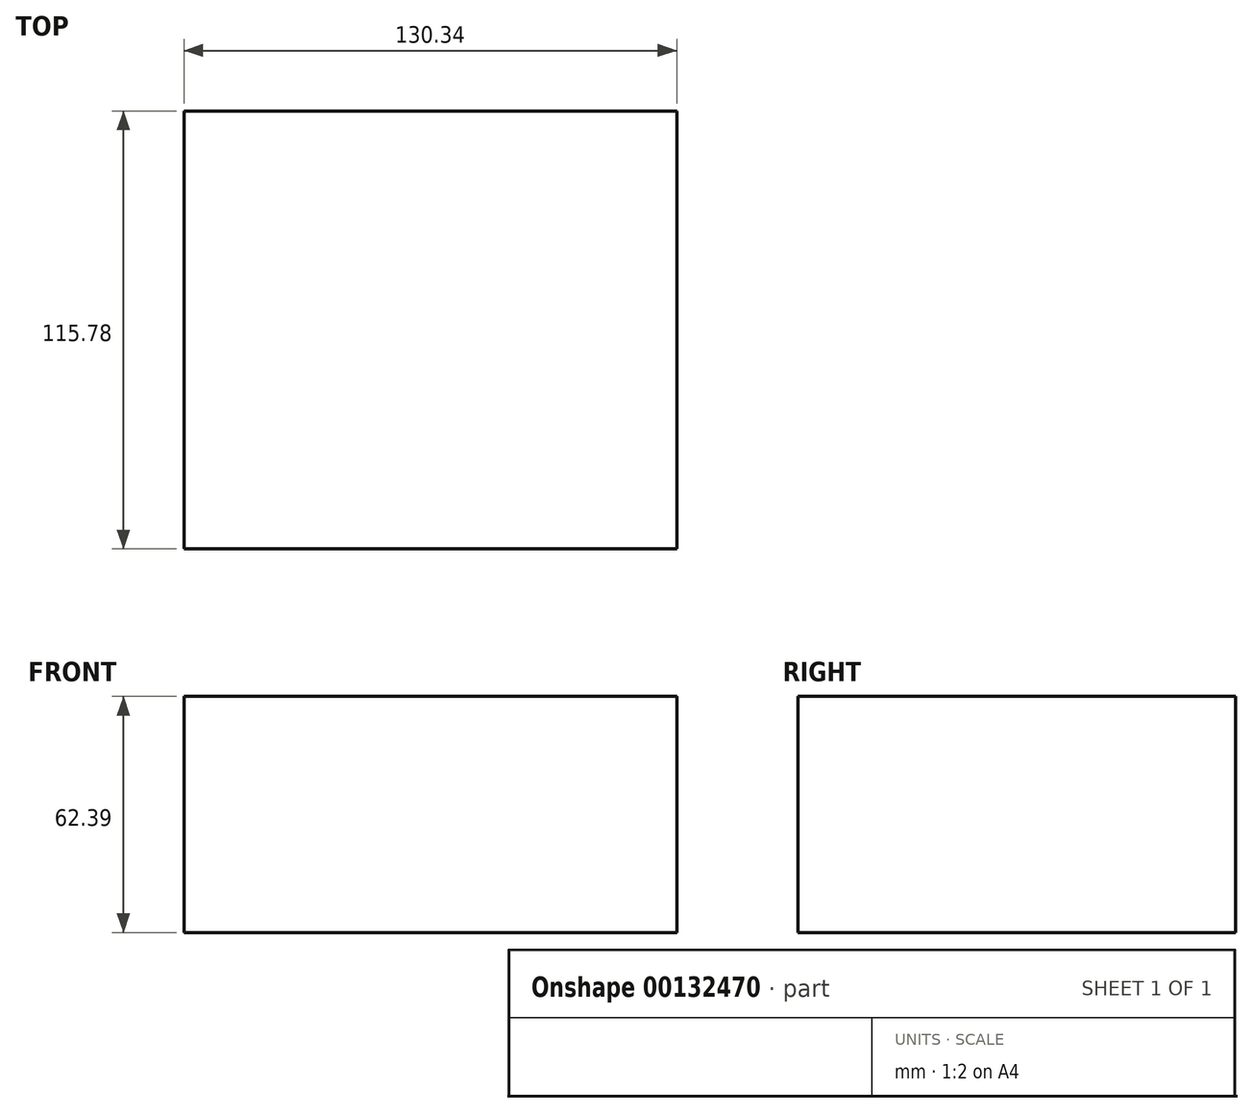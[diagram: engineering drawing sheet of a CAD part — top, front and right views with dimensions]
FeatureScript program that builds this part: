
annotation { "Feature Type Name" : "Feature", "Feature Type Description" : "" }
export const myFeature = defineFeature(function(context is Context, id is Id, definition is map)
    precondition{}
    {
        {
            var Q0;
            Q0=qCreatedBy(makeId("Front.planeOp"),FACE);
            var sketch = newSketch(context, id + "F0", { "sketchPlane" : qUnion([Q0])});
            skLineSegment(sketch, "E0.bottom", {"start": v(-92.43, 0) * mm, "end": v(37.9, 0) * mm});
            skLineSegment(sketch, "E0.top", {"start": v(-92.43, -62.4) * mm, "end": v(37.9, -62.4) * mm});
            skLineSegment(sketch, "E0.left", {"start": v(-92.43, 0) * mm, "end": v(-92.43, -62.4) * mm});
            skLineSegment(sketch, "E0.right", {"start": v(37.9, 0) * mm, "end": v(37.9, -62.4) * mm});
            skSolve(sketch);
        }
        {
            var Q0;
            Q0 = qSketchRegion(id + "F0", true);
            extrude(context, id + "F1", {"entities" : qUnion([Q0]), "oppositeDirection" : true, "depth" : 115.78 * mm});
        }
    });
